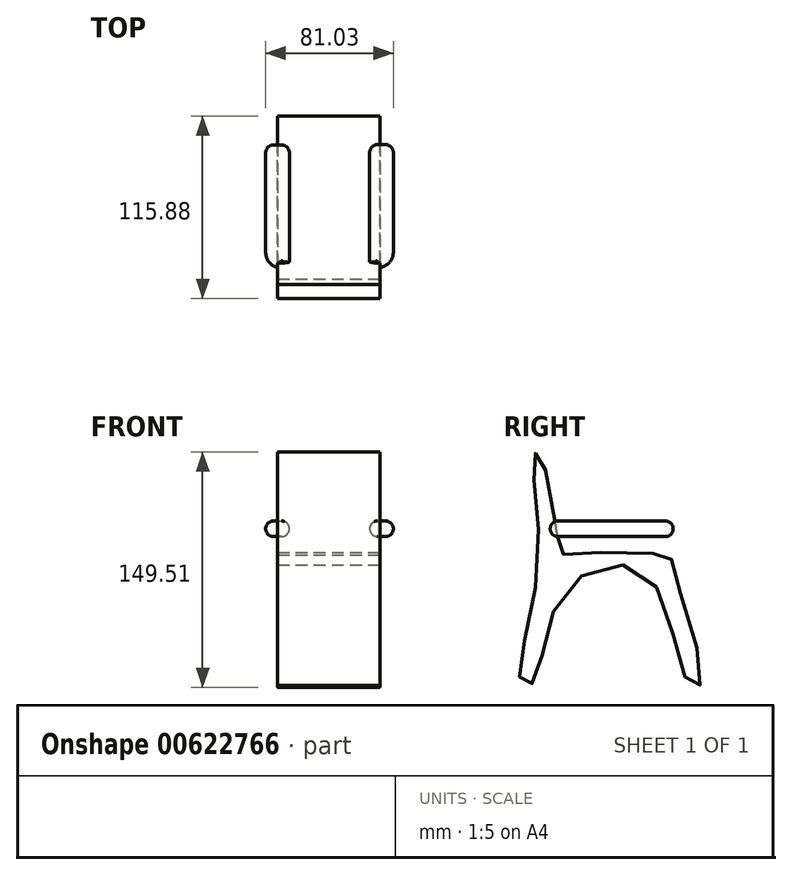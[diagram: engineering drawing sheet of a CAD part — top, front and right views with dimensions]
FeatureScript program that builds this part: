
annotation { "Feature Type Name" : "Feature", "Feature Type Description" : "" }
export const myFeature = defineFeature(function(context is Context, id is Id, definition is map)
    precondition{}
    {
        {
            var Q0;
            Q0=qCreatedBy(makeId("Right.planeOp"),FACE);
            var sketch = newSketch(context, id + "F0", { "sketchPlane" : qUnion([Q0])});
            skFitSpline(sketch, "E0", {"points": [v(-49.55, 69.6) * mm, v(-52.8, 69.03) * mm, v(-50.7, -2.77) * mm, v(-61.4, -75.33) * mm, v(-53.56, -75.71) * mm, v(-35.04, -19.57) * mm, v(18.8, -7.92) * mm, v(44.97, -76.29) * mm, v(52.8, -76.1) * mm, v(34.47, 0) * mm, v(32.18, 4.87) * mm, v(-33.9, 5.63) * mm, v(-36.38, 6.2) * mm, v(-49.55, 69.6) * mm]});
            skSolve(sketch);
        }
        {
            var Q0;
            Q0=makeQuery(id+"F0.imprint","IMPRINT",FACE,{"disambiguationData":[TD([[makeQuery(id+"F0.imprint","IMPRINT",EDGE,{"derivedFrom":sQuery(id+"F0.wireOp",EDGE,"E0")}),1.0]])]});
            var Q1;
            Q1=sQuery(id+"F0.wireOp",EDGE,"E0");
            extrude(context, id + "F1", {"entities" : qUnion([Q0]), "surfaceEntities" : qUnion([Q1]), "depth" : 65 * mm, "offsetDistance" : 25 * mm});
        }
        {
            var Q0;
            Q0=qCreatedBy(makeId("Right.planeOp"),FACE);
            cPlane(context, id + "F2", {"entities" : qUnion([Q0]), "cplaneType" : CPlaneType.OFFSET, "offset" : 65.2 * mm, "width" : 150 * mm, "height" : 150 * mm});
        }
        {
            var Q0;
            Q0=qCreatedBy(makeId("Front.planeOp"),FACE);
            cPlane(context, id + "F3", {"entities" : qUnion([Q0]), "cplaneType" : CPlaneType.OFFSET, "offset" : 42.4 * mm, "width" : 150 * mm, "height" : 150 * mm});
        }
        {
            var Q0;
            Q0=qCreatedBy(id+"F3.planeOp",FACE);
            var sketch = newSketch(context, id + "F4", { "sketchPlane" : qUnion([Q0])});
            skLineSegment(sketch, "E1.bottom", {"start": v(73.53, 26.84) * mm, "end": v(58.53, 26.84) * mm});
            skLineSegment(sketch, "E1.top", {"start": v(73.53, 16.84) * mm, "end": v(58.53, 16.84) * mm});
            skLineSegment(sketch, "E1.left", {"start": v(73.53, 26.84) * mm, "end": v(73.53, 16.84) * mm});
            skLineSegment(sketch, "E1.right", {"start": v(58.53, 26.84) * mm, "end": v(58.53, 16.84) * mm});
            skPoint(sketch, "E1.middle", {"position": v(66.03, 21.84) * mm});
            skLineSegment(sketch, "E2.bottom", {"start": v(7.5, 26.84) * mm, "end": v(-7.5, 26.84) * mm});
            skLineSegment(sketch, "E2.top", {"start": v(7.5, 16.84) * mm, "end": v(-7.5, 16.84) * mm});
            skLineSegment(sketch, "E2.left", {"start": v(7.5, 26.84) * mm, "end": v(7.5, 16.84) * mm});
            skLineSegment(sketch, "E2.right", {"start": v(-7.5, 26.84) * mm, "end": v(-7.5, 16.84) * mm});
            skPoint(sketch, "E2.middle", {"position": v(0, 21.84) * mm});
            skSolve(sketch);
        }
        {
            var Q0;
            Q0=qCreatedBy(id+"F2.planeOp",FACE);
            var sketch = newSketch(context, id + "F5", { "sketchPlane" : qUnion([Q0])});
            skLineSegment(sketch, "E3", {"start": v(-42.53, 21.66) * mm, "end": v(35.2, 21.66) * mm});
            skSolve(sketch);
        }
        {
            var Q0;
            Q0=makeQuery(id+"F4.imprint","IMPRINT",FACE,{"disambiguationData":[TD([[makeQuery(id+"F4.imprint","IMPRINT",EDGE,{"derivedFrom":sQuery(id+"F4.wireOp",EDGE,"E1.bottom")}),1.0]])]});
            var Q1;
            Q1=sQuery(id+"F5.wireOp",EDGE,"E3");
            sweep(context, id + "F6", {"operationType" : NewBodyOperationType.ADD, "profiles" : qUnion([Q0]), "path" : qUnion([Q1])});
        }
        {
            var Q0;
            Q0=makeQuery(id+"F6.opSweep","CAP_EDGE",EDGE,{"disambiguationData":[OSD([sQuery(id+"F4.wireOp",EDGE,"E1.left"),sQuery(id+"F5.wireOp",VERTEX,"E3.start")])],"isStart":false});
            fillet(context, id + "F7", {"entities" : qUnion([Q0]), "radius" : 10 * mm, "tangentPropagation" : true, "allowEdgeOverflow" : false});
        }
        {
            var Q0;
            Q0=qCreatedBy(makeId("Right.planeOp"),FACE);
            var sketch = newSketch(context, id + "F8", { "sketchPlane" : qUnion([Q0])});
            skLineSegment(sketch, "E4", {"start": v(35, 21.86) * mm, "end": v(-42.91, 21.86) * mm});
            skSolve(sketch);
        }
        {
            var Q0;
            Q0 = qSketchRegion(id + "F4", true);
            var Q1;
            Q1=sQuery(id+"F8.wireOp",EDGE,"E4");
            sweep(context, id + "F9", {"operationType" : NewBodyOperationType.ADD, "profiles" : qUnion([Q0]), "path" : qUnion([Q1])});
        }
        {
            var Q0;
            Q0=makeQuery(id+"F9.opSweep","CAP_EDGE",EDGE,{"disambiguationData":[OSD([sQuery(id+"F4.wireOp",EDGE,"E2.right"),sQuery(id+"F8.wireOp",VERTEX,"E4.end")])],"isStart":false});
            fillet(context, id + "F10", {"entities" : qUnion([Q0]), "radius" : 10 * mm, "tangentPropagation" : true, "allowEdgeOverflow" : false});
        }
        {
            var Q0;
            Q0=makeQuery(id+"F9.opSweep","CAP_EDGE",EDGE,{"disambiguationData":[OSD([sQuery(id+"F4.wireOp",EDGE,"E2.bottom"),sQuery(id+"F8.wireOp",VERTEX,"E4.start")])],"isStart":true});
            var Q1;
            Q1=makeQuery(id+"F9.opSweep","CAP_EDGE",EDGE,{"disambiguationData":[OSD([sQuery(id+"F4.wireOp",EDGE,"E2.top"),sQuery(id+"F8.wireOp",VERTEX,"E4.start")])],"isStart":true});
            var Q2;
            Q2=makeQuery(id+"F6.opSweep","CAP_EDGE",EDGE,{"disambiguationData":[OSD([sQuery(id+"F4.wireOp",EDGE,"E1.bottom"),sQuery(id+"F5.wireOp",VERTEX,"E3.end")])],"isStart":true});
            var Q3;
            Q3=makeQuery(id+"F6.opSweep","CAP_EDGE",EDGE,{"disambiguationData":[OSD([sQuery(id+"F4.wireOp",EDGE,"E1.top"),sQuery(id+"F5.wireOp",VERTEX,"E3.end")])],"isStart":true});
            fillet(context, id + "F11", {"entities" : qUnion([Q0, Q1, Q2, Q3]), "radius" : 5 * mm, "tangentPropagation" : true, "allowEdgeOverflow" : false});
        }
        {
            var Q0;
            Q0=makeQuery(id+"F9.opSweep","CAP_EDGE",EDGE,{"disambiguationData":[OSD([sQuery(id+"F4.wireOp",EDGE,"E1.left"),sQuery(id+"F8.wireOp",VERTEX,"E4.end")])],"isStart":false});
            fillet(context, id + "F12", {"entities" : qUnion([Q0]), "radius" : 10 * mm, "tangentPropagation" : true, "allowEdgeOverflow" : false});
        }
        {
            var Q0;
            {var subQ0=sQuery(id+"F4.wireOp",EDGE,"E1.left");var subQ1=sQuery(id+"F4.wireOp",EDGE,"E1.top");Q0=makeQuery(id+"F9.boolean.opBoolean","MERGE",EDGE,{"derivedFrom":[makeQuery(id+"F6.opSweep","SWEPT_EDGE",EDGE,{"disambiguationData":[OSD([subQ1,subQ0,sQuery(id+"F5.wireOp",EDGE,"E3")])]}),makeQuery(id+"F9.opSweep","SWEPT_EDGE",EDGE,{"disambiguationData":[OSD([subQ1,subQ0,sQuery(id+"F8.wireOp",EDGE,"E4")])]})]});}
            var Q1;
            {var subQ0=sQuery(id+"F4.wireOp",EDGE,"E1.left");var subQ1=sQuery(id+"F4.wireOp",EDGE,"E1.bottom");Q1=makeQuery(id+"F9.boolean.opBoolean","MERGE",EDGE,{"derivedFrom":[makeQuery(id+"F6.opSweep","SWEPT_EDGE",EDGE,{"disambiguationData":[OSD([subQ1,subQ0,sQuery(id+"F5.wireOp",EDGE,"E3")])]}),makeQuery(id+"F9.opSweep","SWEPT_EDGE",EDGE,{"disambiguationData":[OSD([subQ1,subQ0,sQuery(id+"F8.wireOp",EDGE,"E4")])]})]});}
            fillet(context, id + "F13", {"entities" : qUnion([Q0, Q1]), "radius" : 5 * mm, "tangentPropagation" : true, "allowEdgeOverflow" : false});
        }
        {
            var Q0;
            Q0=makeQuery(id+"F9.opSweep","SWEPT_EDGE",EDGE,{"disambiguationData":[OSD([sQuery(id+"F4.wireOp",EDGE,"E2.bottom"),sQuery(id+"F4.wireOp",EDGE,"E2.right"),sQuery(id+"F8.wireOp",EDGE,"E4")])]});
            var Q1;
            Q1=makeQuery(id+"F9.opSweep","SWEPT_EDGE",EDGE,{"disambiguationData":[OSD([sQuery(id+"F4.wireOp",EDGE,"E2.top"),sQuery(id+"F4.wireOp",EDGE,"E2.right"),sQuery(id+"F8.wireOp",EDGE,"E4")])]});
            fillet(context, id + "F14", {"entities" : qUnion([Q0, Q1]), "radius" : 5 * mm, "tangentPropagation" : true, "allowEdgeOverflow" : false});
        }
        {
            var Q0;
            Q0=makeQuery(id+"F6.opSweep","SWEPT_EDGE",EDGE,{"disambiguationData":[OSD([sQuery(id+"F4.wireOp",EDGE,"E1.bottom"),sQuery(id+"F4.wireOp",EDGE,"E1.right"),sQuery(id+"F5.wireOp",EDGE,"E3")])]});
            var Q1;
            Q1=makeQuery(id+"F6.opSweep","SWEPT_EDGE",EDGE,{"disambiguationData":[OSD([sQuery(id+"F4.wireOp",EDGE,"E1.top"),sQuery(id+"F4.wireOp",EDGE,"E1.right"),sQuery(id+"F5.wireOp",EDGE,"E3")])]});
            fillet(context, id + "F15", {"entities" : qUnion([Q0, Q1]), "radius" : 5 * mm, "tangentPropagation" : true, "allowEdgeOverflow" : false});
        }
        {
            var Q0;
            Q0=makeQuery(id+"F9.opSweep","SWEPT_EDGE",EDGE,{"disambiguationData":[OSD([sQuery(id+"F4.wireOp",EDGE,"E2.bottom"),sQuery(id+"F4.wireOp",EDGE,"E2.left"),sQuery(id+"F8.wireOp",EDGE,"E4")])]});
            var Q1;
            Q1=makeQuery(id+"F9.opSweep","SWEPT_EDGE",EDGE,{"disambiguationData":[OSD([sQuery(id+"F4.wireOp",EDGE,"E2.top"),sQuery(id+"F4.wireOp",EDGE,"E2.left"),sQuery(id+"F8.wireOp",EDGE,"E4")])]});
            fillet(context, id + "F16", {"entities" : qUnion([Q0, Q1]), "radius" : 5 * mm, "tangentPropagation" : true, "allowEdgeOverflow" : false});
        }
    });
